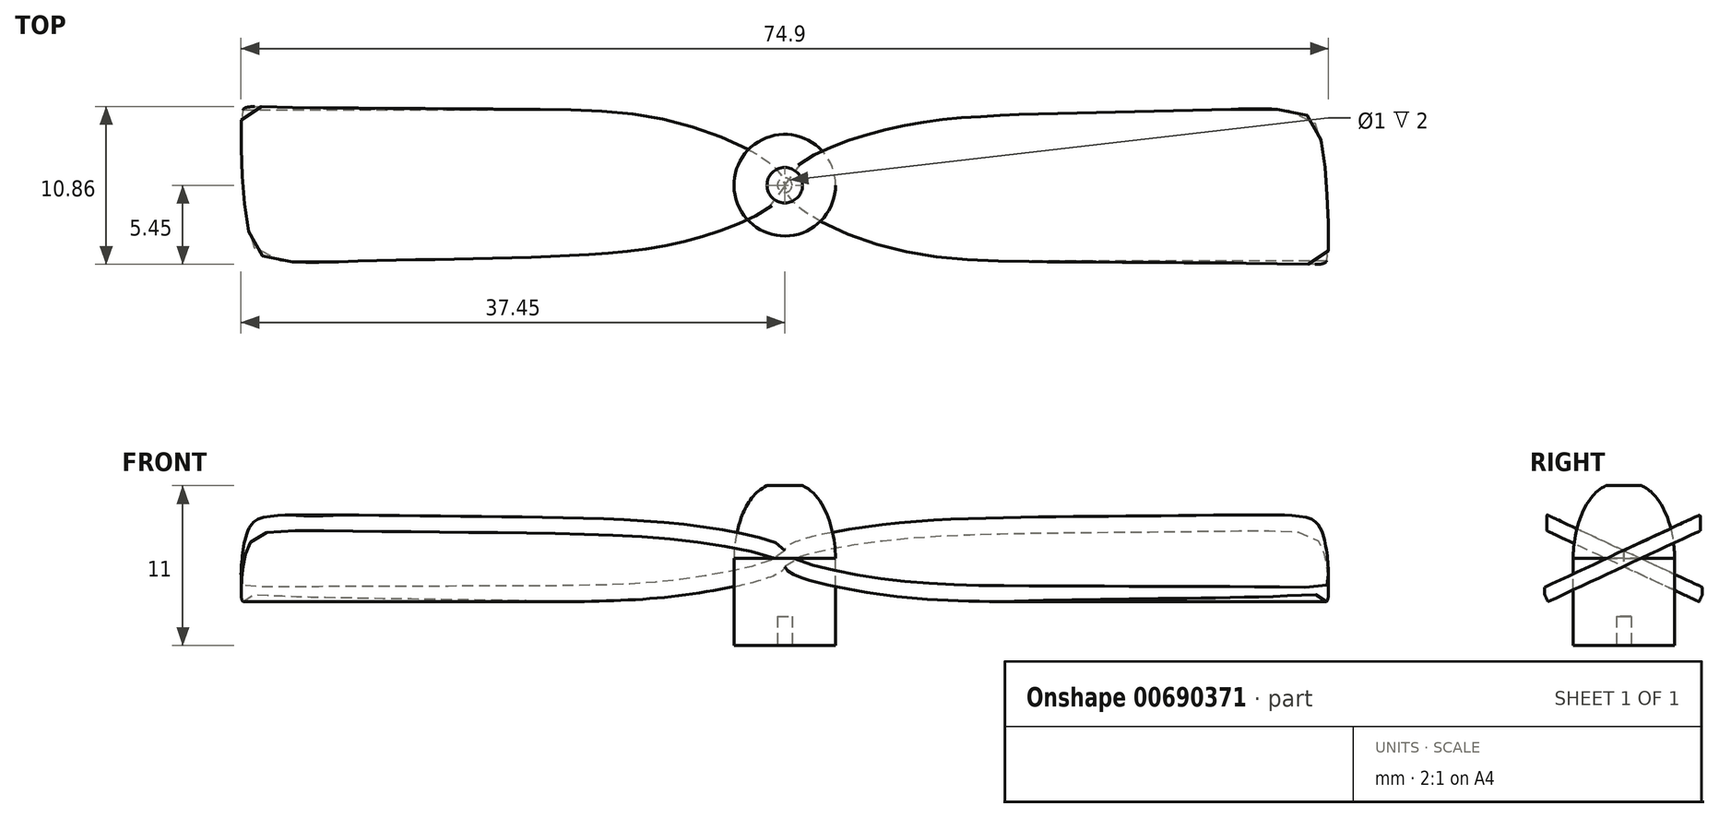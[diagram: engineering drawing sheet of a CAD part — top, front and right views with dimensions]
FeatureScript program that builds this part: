
annotation { "Feature Type Name" : "Feature", "Feature Type Description" : "" }
export const myFeature = defineFeature(function(context is Context, id is Id, definition is map)
    precondition{}
    {
        {
            var Q0;
            Q0=qCreatedBy(makeId("Right.planeOp"),FACE);
            var sketch = newSketch(context, id + "F0", { "sketchPlane" : qUnion([Q0])});
            skLineSegment(sketch, "E0", {"start": v(-5.65, 3.92) * mm, "end": v(5.23, 8.99) * mm});
            skLineSegment(sketch, "E1", {"start": v(5.23, 8.99) * mm, "end": v(5.65, 8.08) * mm});
            skLineSegment(sketch, "E2", {"start": v(5.65, 8.08) * mm, "end": v(-5.23, 3.01) * mm});
            skLineSegment(sketch, "E3", {"start": v(-5.23, 3.01) * mm, "end": v(-5.65, 3.92) * mm});
            skLineSegment(sketch, "E4", {"start": v(0, 0) * mm, "end": v(0, 6) * mm, "construction": true});
            skLineSegment(sketch, "E5", {"start": v(-5.23, 3.01) * mm, "end": v(-5.23, -13.05) * mm, "construction": true});
            skLineSegment(sketch, "E6", {"start": v(-5.23, -13.05) * mm, "end": v(5.23, -13.05) * mm, "construction": true});
            skLineSegment(sketch, "E7", {"start": v(-0.21, 6.45) * mm, "end": v(0.21, 5.55) * mm});
            skLineSegment(sketch, "E8", {"start": v(5.23, -13.05) * mm, "end": v(5.23, 8.99) * mm, "construction": true});
            skSolve(sketch);
        }
        {
            var Q0;
            Q0 = qSketchRegion(id + "F0", true);
            extrude(context, id + "F1", {"entities" : qUnion([Q0]), "depth" : 37.5 * mm, "offsetDistance" : 25.4 * mm});
        }
        {
            var Q0;
            Q0=qCreatedBy(makeId("Top.planeOp"),FACE);
            var sketch = newSketch(context, id + "F2", { "sketchPlane" : qUnion([Q0])});
            skFitSpline(sketch, "E9", {"points": [v(0, 0) * mm, v(5.55, 3.45) * mm, v(13.82, 4.75) * mm, v(22.26, 5.03) * mm, v(29.42, 5.19) * mm, v(35.5, 5.02) * mm, v(36.5, 4.28) * mm, v(37.16, 1.66) * mm, v(37.39, -4.93) * mm, v(37.16, -5.37) * mm, v(35.24, -5.43) * mm, v(17.67, -5.27) * mm, v(6.12, -4) * mm, v(0, 0) * mm]});
            skLineSegment(sketch, "E10.bottom", {"start": v(43.66, 21.32) * mm, "end": v(-43.66, 21.32) * mm});
            skLineSegment(sketch, "E10.top", {"start": v(43.66, -21.32) * mm, "end": v(-43.66, -21.32) * mm});
            skLineSegment(sketch, "E10.left", {"start": v(43.66, 21.32) * mm, "end": v(43.66, -21.32) * mm});
            skLineSegment(sketch, "E10.right", {"start": v(-43.66, 21.32) * mm, "end": v(-43.66, -21.32) * mm});
            skSolve(sketch);
        }
        {
            var Q0;
            Q0 = qSketchRegion(id + "F2", true);
            extrude(context, id + "F3", {"entities" : qUnion([Q0]), "operationType" : NewBodyOperationType.REMOVE, "depth" : 20 * mm, "offsetDistance" : 25.4 * mm});
        }
        {
            var Q0;
            Q0=makeQuery(id+"F1.opExtrude","SWEPT_BODY",BODY,{"disambiguationData":[OSD([sQuery(id+"F0.wireOp",EDGE,"E0"),sQuery(id+"F0.wireOp",EDGE,"E1"),sQuery(id+"F0.wireOp",EDGE,"E2"),sQuery(id+"F0.wireOp",EDGE,"E3")])]});
            var Q1;
            Q1=makeQuery(id+"F3.boolean.opBoolean","INTERSECT",EDGE,{"disambiguationData":[OD(0.0)],"derivedFrom":[makeQuery(id+"F1.opExtrude","CAP_FACE",FACE,{"disambiguationData":[OSD([sQuery(id+"F0.wireOp",EDGE,"E0"),sQuery(id+"F0.wireOp",EDGE,"E1"),sQuery(id+"F0.wireOp",EDGE,"E2"),sQuery(id+"F0.wireOp",EDGE,"E3")])],"isStart":true}),makeQuery(id+"F3.opExtrude","SWEPT_FACE",FACE,{"disambiguationData":[OSD([sQuery(id+"F2.wireOp",EDGE,"E9")])]})]});
            circularPattern(context, id + "F4", {"entities" : qUnion([Q0]), "axis" : qUnion([Q1]), "angle" : 360 * degree, "instanceCount" : 2, "equalSpace" : true});
        }
        {
            var Q0;
            Q0=qCreatedBy(makeId("Front.planeOp"),FACE);
            var sketch = newSketch(context, id + "F5", { "sketchPlane" : qUnion([Q0])});
            skLineSegment(sketch, "E11", {"start": v(0, 0) * mm, "end": v(-3.5, 0) * mm});
            skLineSegment(sketch, "E12", {"start": v(-3.5, 0) * mm, "end": v(-3.5, 6) * mm});
            skFitSpline(sketch, "E13", {"points": [v(-3.5, 6) * mm, v(-1.22, 11) * mm], "startDerivative": vector(0.09, 5.63) * mm, "endDerivative": vector(4.68, 2.03) * mm});
            skLineSegment(sketch, "E14", {"start": v(-1.22, 11) * mm, "end": v(0, 11) * mm});
            skLineSegment(sketch, "E15", {"start": v(0, 11) * mm, "end": v(0, 0) * mm});
            skSolve(sketch);
        }
        {
            var Q0;
            Q0=makeQuery(id+"F5.imprint","IMPRINT",FACE,{"disambiguationData":[TD([[makeQuery(id+"F5.imprint","IMPRINT",EDGE,{"derivedFrom":sQuery(id+"F5.wireOp",EDGE,"E11")}),-1.0]])]});
            var Q1;
            Q1=sQuery(id+"F5.wireOp",EDGE,"E15");
            revolve(context, id + "F6", {"entities" : qUnion([Q0]), "axis" : qUnion([Q1]), "revolveType" : RevolveType.FULL});
        }
        {
            var Q0;
            Q0=makeQuery(id+"F6.opRevolve","SWEPT_FACE",FACE,{"disambiguationData":[OSD([sQuery(id+"F5.wireOp",EDGE,"E11")])]});
            var sketch = newSketch(context, id + "F7", { "sketchPlane" : qUnion([Q0])});
            skCircle(sketch, "E16", {"center": v(0, 0) * mm, "radius": 0.5 * mm});
            skSolve(sketch);
        }
        {
            var Q0;
            Q0 = qSketchRegion(id + "F7", true);
            extrude(context, id + "F8", {"entities" : qUnion([Q0]), "operationType" : NewBodyOperationType.REMOVE, "oppositeDirection" : true, "depth" : 2 * mm, "offsetDistance" : 25.4 * mm});
        }
    });
